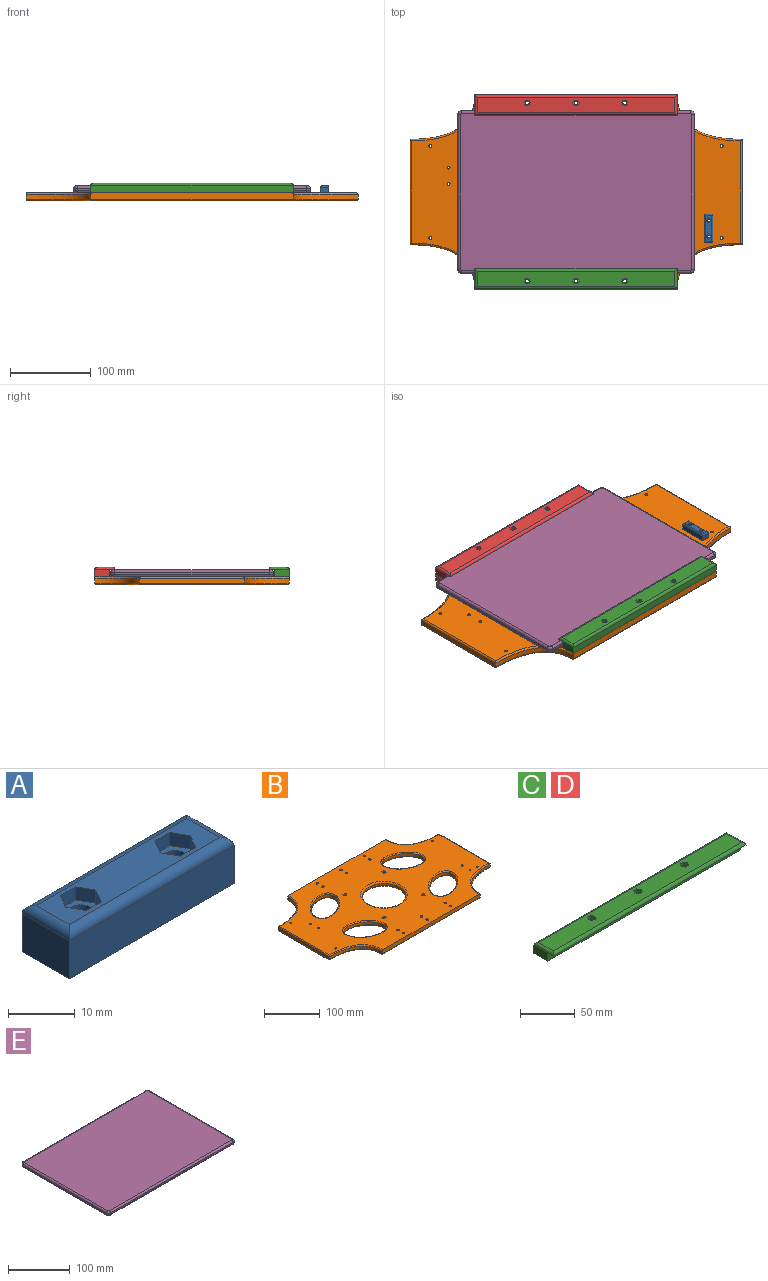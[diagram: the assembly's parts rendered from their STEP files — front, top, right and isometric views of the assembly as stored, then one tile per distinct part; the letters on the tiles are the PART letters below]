
ASSEMBLY  parts=5 mates=4
PART A: 26 faces, bbox 35x10x8.5 mm
  f0: cylinder r=1.8mm len=6.1mm, axis (0,0,1), area 69mm2, adj f6,f25
  f1: cylinder r=1.8mm len=6.1mm, axis (0,0,1), area 69mm2, adj f6,f18
  f2: plane 35x7mm, normal (0,-1,0), area 245mm2, adj f3,f5,f6,f8
  f3: plane 10x7mm, normal (1,0,0), area 70mm2, adj f2,f4,f6,f9
  f4: plane 35x7mm, normal (0,1,0), area 245mm2, adj f3,f5,f6,f11
  f5: plane 10x7mm, normal (-1,0,0), area 70mm2, adj f2,f4,f6,f10
  f6: plane 35x10mm, normal (0,0,-1), area 329.6mm2, adj f0,f1,f2,f3,f4,f5
  f7: plane 32x7mm, normal (0,0,1), area 171.6mm2, adj f8,f9,f10,f11,f12,f13,f14,f15
  f8: cylinder r=1.5mm len=35mm, axis (1,0,0), area 79.9mm2, adj f2,f7,f9,f10
  f9: cylinder r=1.5mm len=10mm, axis (0,1,0), area 21mm2, adj f3,f7,f8,f11
  f10: cylinder r=1.5mm len=10mm, axis (0,-1,0), area 21mm2, adj f5,f7,f8,f11
  f11: cylinder r=1.5mm len=35mm, axis (-1,0,0), area 79.9mm2, adj f4,f7,f9,f10
  f12: plane 2.75x2.4mm, normal (-0.87,0.5,0), area 7.6mm2, adj f7,f13,f17,f18
  f13: plane 2.75x2.4mm, normal (-0.87,-0.5,0), area 7.6mm2, adj f7,f12,f14,f18
  f14: plane 3.18x2.4mm, normal (0,-1,0), area 7.6mm2, adj f7,f13,f15,f18
  f15: plane 2.75x2.4mm, normal (0.87,-0.5,0), area 7.6mm2, adj f7,f14,f16,f18
  f16: plane 2.75x2.4mm, normal (0.87,0.5,0), area 7.6mm2, adj f7,f15,f17,f18
  f17: plane 3.18x2.4mm, normal (0,1,0), area 7.6mm2, adj f7,f12,f16,f18
  f18: plane 6.35x5.5mm, normal (0,0,1), area 16mm2, adj f1,f12,f13,f14,f15,f16,f17
  f19: plane 2.75x2.4mm, normal (0.87,-0.5,0), area 7.6mm2, adj f7,f20,f24,f25
  f20: plane 2.75x2.4mm, normal (0.87,0.5,0), area 7.6mm2, adj f7,f19,f21,f25
  f21: plane 3.18x2.4mm, normal (0,1,0), area 7.6mm2, adj f7,f20,f22,f25
  f22: plane 2.75x2.4mm, normal (-0.87,0.5,0), area 7.6mm2, adj f7,f21,f23,f25
  f23: plane 2.75x2.4mm, normal (-0.87,-0.5,0), area 7.6mm2, adj f7,f22,f24,f25
  f24: plane 3.18x2.4mm, normal (0,-1,0), area 7.6mm2, adj f7,f19,f23,f25
  f25: plane 6.35x5.5mm, normal (0,0,1), area 16mm2, adj f0,f19,f20,f21,f22,f23,f24
PART B: 123 faces, bbox 413.3x241.5x10.1 mm
  f0: plane 406.06x240.06mm, normal (0,0,1), area 63187.4mm2, adj f8,f15,f18,f29,f30,f31,f32,f33
  f1: cylinder r=2.4mm len=6mm, axis (0,0,1), area 90.5mm2, adj f9,f86
  f2: cylinder r=2.4mm len=6mm, axis (0,0,1), area 90.5mm2, adj f9,f79
  f3: cylinder r=2.4mm len=6mm, axis (0,0,1), area 90.5mm2, adj f9,f72
  f4: cylinder r=2.4mm len=6mm, axis (0,0,1), area 90.5mm2, adj f9,f65
  f5: extruded ~80x55mm, area 661.9mm2, adj f6,f8,f20,f29
  f6: plane 130x6mm, normal (-1,0,0), area 780mm2, adj f5,f13,f22,f30
  f7: extruded ~70.11x57.36mm, area 1193.2mm2, adj f38,f39
  f8: plane 250.06x8.06mm, normal (0,1,0), area 1998.3mm2, adj f0,f5,f10,f21,f29,f33
  f9: plane 406.06x236.06mm, normal (0,0,-1), area 61751.9mm2, adj f1,f2,f3,f4,f19,f20,f21,f22
  f10: extruded ~80x55mm, area 661.9mm2, adj f8,f11,f23,f33
  f11: plane 130x6mm, normal (1,0,0), area 780mm2, adj f10,f16,f25,f34
  f12: extruded ~70.3x57.3mm, area 1193.2mm2, adj f36,f37
  f13: extruded ~80x55mm, area 661.9mm2, adj f6,f15,f24,f31
  f14: extruded ~70.3x57.3mm, area 1193.2mm2, adj f18,f28
  f15: plane 250.06x8.06mm, normal (0,-1,0), area 1998.3mm2, adj f0,f13,f16,f26,f31,f35
  f16: extruded ~80x55mm, area 661.9mm2, adj f11,f15,f27,f35
  f17: extruded ~70.11x57.36mm, area 1193.2mm2, adj f19,f32
  f18: bspline ~74.32x61.43mm, area 639.2mm2, adj f0,f14
  f19: bspline ~74.35x61.42mm, area 639.2mm2, adj f9,f17
  f20: bspline ~83.64x57.72mm, area 343.9mm2, adj f5,f9,f21,f22
  f21: cylinder r=2mm len=250mm, axis (-1,0,0), area 779.2mm2, adj f8,f9,f20,f23
  f22: cylinder r=2mm len=130mm, axis (0,-1,0), area 402.2mm2, adj f6,f9,f20,f24
  f23: bspline ~83.64x57.72mm, area 343.9mm2, adj f9,f10,f21,f25
  f24: bspline ~83.64x57.72mm, area 343.9mm2, adj f9,f13,f22,f26
  f25: cylinder r=2mm len=130mm, axis (0,-1,0), area 402.2mm2, adj f9,f11,f23,f27
  f26: cylinder r=2mm len=250mm, axis (-1,0,0), area 779.2mm2, adj f9,f15,f24,f27
  f27: bspline ~83.64x57.72mm, area 343.9mm2, adj f9,f16,f25,f26
  f28: bspline ~74.35x61.42mm, area 639.2mm2, adj f9,f14
  f29: bspline ~83.64x57.72mm, area 347mm2, adj f0,f5,f8,f30
  f30: cylinder r=2mm len=130mm, axis (0,1,0), area 402.2mm2, adj f0,f6,f29,f31
  f31: bspline ~83.64x57.72mm, area 347mm2, adj f0,f13,f15,f30
  f32: bspline ~74.32x61.43mm, area 639.2mm2, adj f0,f17
  f33: bspline ~83.64x57.72mm, area 347mm2, adj f0,f8,f10,f34
  f34: cylinder r=2mm len=130mm, axis (0,1,0), area 402.2mm2, adj f0,f11,f33,f35
  f35: bspline ~83.64x57.72mm, area 347mm2, adj f0,f15,f16,f34
  f36: bspline ~74.32x61.43mm, area 639.2mm2, adj f0,f12
  f37: bspline ~74.35x61.42mm, area 639.2mm2, adj f9,f12
  f38: bspline ~74.35x61.42mm, area 639.2mm2, adj f7,f9
  f39: bspline ~74.32x61.43mm, area 639.2mm2, adj f0,f7
  f40: cylinder r=1.8mm len=10mm, axis (0,0,1), area 113.1mm2, adj f0,f9
  f41: cylinder r=1.8mm len=10mm, axis (0,0,1), area 113.1mm2, adj f0,f9
  f42: cylinder r=1.8mm len=10mm, axis (0,0,1), area 113.1mm2, adj f0,f9
  f43: cylinder r=1.8mm len=10mm, axis (0,0,1), area 113.1mm2, adj f0,f9
  f44: cylinder r=39.02mm len=78.04mm, axis (0,0,1), area 980.6mm2, adj f45,f46
  f45: torus R=42.02mm, axis (0,0,1), area 1187.5mm2, adj f9,f44
  f46: torus R=42.02mm, axis (0,0,1), area 1187.5mm2, adj f0,f44
  f47: cylinder r=1.7mm len=7mm, axis (0,0,-1), area 74.8mm2, adj f0,f48
  f48: plane 6.5x6.5mm, normal (0,0,-1), area 24.1mm2, adj f47,f49
  f49: cylinder r=3.25mm len=6.5mm, axis (0,0,-1), area 61.3mm2, adj f9,f48
  f50: cylinder r=1.7mm len=7mm, axis (0,0,-1), area 74.8mm2, adj f0,f51
  f51: plane 6.5x6.5mm, normal (0,0,-1), area 24.1mm2, adj f50,f52
  f52: cylinder r=3.25mm len=6.5mm, axis (0,0,-1), area 61.3mm2, adj f9,f51
  f53: cylinder r=1.7mm len=7mm, axis (0,0,-1), area 74.8mm2, adj f0,f54
  f54: plane 6.5x6.5mm, normal (0,0,-1), area 24.1mm2, adj f53,f55
  f55: cylinder r=3.25mm len=6.5mm, axis (0,0,-1), area 61.3mm2, adj f9,f54
  f56: cylinder r=1.7mm len=7mm, axis (0,0,-1), area 74.8mm2, adj f0,f57
  f57: plane 6.5x6.5mm, normal (0,0,-1), area 24.1mm2, adj f56,f58
  f58: cylinder r=3.25mm len=6.5mm, axis (0,0,-1), area 61.3mm2, adj f9,f57
  f59: plane 4x3.5mm, normal (-0.87,0.5,0), area 16.2mm2, adj f0,f60,f64,f65
  f60: plane 4x3.5mm, normal (-0.87,-0.5,0), area 16.2mm2, adj f0,f59,f61,f65
  f61: plane 4.04x4mm, normal (0,-1,0), area 16.2mm2, adj f0,f60,f62,f65
  f62: plane 4x3.5mm, normal (0.87,-0.5,0), area 16.2mm2, adj f0,f61,f63,f65
  f63: plane 4x3.5mm, normal (0.87,0.5,0), area 16.2mm2, adj f0,f62,f64,f65
  f64: plane 4.04x4mm, normal (0,1,0), area 16.2mm2, adj f0,f59,f63,f65
  f65: plane 8.08x7mm, normal (0,0,1), area 24.3mm2, adj f4,f59,f60,f61,f62,f63,f64
  f66: plane 4x3.5mm, normal (-0.87,-0.5,0), area 16.2mm2, adj f0,f67,f71,f72
  f67: plane 4.04x4mm, normal (0,-1,0), area 16.2mm2, adj f0,f66,f68,f72
  f68: plane 4x3.5mm, normal (0.87,-0.5,0), area 16.2mm2, adj f0,f67,f69,f72
  f69: plane 4x3.5mm, normal (0.87,0.5,0), area 16.2mm2, adj f0,f68,f70,f72
  f70: plane 4.04x4mm, normal (0,1,0), area 16.2mm2, adj f0,f69,f71,f72
  f71: plane 4x3.5mm, normal (-0.87,0.5,0), area 16.2mm2, adj f0,f66,f70,f72
  f72: plane 8.08x7mm, normal (0,0,1), area 24.3mm2, adj f3,f66,f67,f68,f69,f70,f71
  f73: plane 4x3.5mm, normal (0.87,-0.5,0), area 16.2mm2, adj f0,f74,f78,f79
  f74: plane 4x3.5mm, normal (0.87,0.5,0), area 16.2mm2, adj f0,f73,f75,f79
  f75: plane 4.04x4mm, normal (0,1,0), area 16.2mm2, adj f0,f74,f76,f79
  f76: plane 4x3.5mm, normal (-0.87,0.5,0), area 16.2mm2, adj f0,f75,f77,f79
  f77: plane 4x3.5mm, normal (-0.87,-0.5,0), area 16.2mm2, adj f0,f76,f78,f79
  f78: plane 4.04x4mm, normal (0,-1,0), area 16.2mm2, adj f0,f73,f77,f79
  f79: plane 8.08x7mm, normal (0,0,1), area 24.3mm2, adj f2,f73,f74,f75,f76,f77,f78
  f80: plane 4.04x4mm, normal (0,1,0), area 16.2mm2, adj f0,f81,f85,f86
  f81: plane 4x3.5mm, normal (-0.87,0.5,0), area 16.2mm2, adj f0,f80,f82,f86
  f82: plane 4x3.5mm, normal (-0.87,-0.5,0), area 16.2mm2, adj f0,f81,f83,f86
  f83: plane 4.04x4mm, normal (0,-1,0), area 16.2mm2, adj f0,f82,f84,f86
  f84: plane 4x3.5mm, normal (0.87,-0.5,0), area 16.2mm2, adj f0,f83,f85,f86
  f85: plane 4x3.5mm, normal (0.87,0.5,0), area 16.2mm2, adj f0,f80,f84,f86
  f86: plane 8.08x7mm, normal (0,0,1), area 24.3mm2, adj f1,f80,f81,f82,f83,f84,f85
  f87: cylinder r=2.25mm len=6mm, axis (0,0,-1), area 84.8mm2, adj f0,f88
  f88: plane 8.25x8.25mm, normal (0,0,-1), area 37.6mm2, adj f87,f89
  f89: cylinder r=4.12mm len=8.25mm, axis (0,0,-1), area 103.7mm2, adj f9,f88
  f90: cylinder r=2.25mm len=6mm, axis (0,0,-1), area 84.8mm2, adj f0,f91
  f91: plane 8.25x8.25mm, normal (0,0,-1), area 37.6mm2, adj f90,f92
  f92: cylinder r=4.12mm len=8.25mm, axis (0,0,-1), area 103.7mm2, adj f9,f91
  f93: cylinder r=2.25mm len=6mm, axis (0,0,-1), area 84.8mm2, adj f0,f94
  f94: plane 8.25x8.25mm, normal (0,0,-1), area 37.6mm2, adj f93,f95
  f95: cylinder r=4.12mm len=8.25mm, axis (0,0,-1), area 103.7mm2, adj f9,f94
  f96: cylinder r=2.25mm len=6mm, axis (0,0,-1), area 84.8mm2, adj f0,f97
  f97: plane 8.25x8.25mm, normal (0,0,-1), area 37.6mm2, adj f96,f98
  f98: cylinder r=4.12mm len=8.25mm, axis (0,0,-1), area 103.7mm2, adj f9,f97
  f99: cylinder r=2.25mm len=6mm, axis (0,0,-1), area 84.8mm2, adj f0,f100
  f100: plane 8.25x8.25mm, normal (0,0,-1), area 37.6mm2, adj f99,f101
  f101: cylinder r=4.12mm len=8.25mm, axis (0,0,-1), area 103.7mm2, adj f9,f100
  f102: cylinder r=2.25mm len=6mm, axis (0,0,-1), area 84.8mm2, adj f0,f103
  f103: plane 8.25x8.25mm, normal (0,0,-1), area 37.6mm2, adj f102,f104
  f104: cylinder r=4.12mm len=8.25mm, axis (0,0,-1), area 103.7mm2, adj f9,f103
  f105: cylinder r=2.25mm len=6mm, axis (0,0,-1), area 84.8mm2, adj f0,f106
  f106: plane 8.25x8.25mm, normal (0,0,-1), area 37.6mm2, adj f105,f107
  f107: cylinder r=4.12mm len=8.25mm, axis (0,0,-1), area 103.7mm2, adj f9,f106
  f108: cylinder r=2.25mm len=6mm, axis (0,0,-1), area 84.8mm2, adj f0,f109
  f109: plane 8.25x8.25mm, normal (0,0,-1), area 37.6mm2, adj f108,f110
  f110: cylinder r=4.12mm len=8.25mm, axis (0,0,-1), area 103.7mm2, adj f9,f109
  f111: cylinder r=2.25mm len=6mm, axis (0,0,-1), area 84.8mm2, adj f0,f112
  f112: plane 8.25x8.25mm, normal (0,0,-1), area 37.6mm2, adj f111,f113
  f113: cylinder r=4.12mm len=8.25mm, axis (0,0,-1), area 103.7mm2, adj f9,f112
  f114: cylinder r=2.25mm len=6mm, axis (0,0,-1), area 84.8mm2, adj f0,f115
  f115: plane 8.25x8.25mm, normal (0,0,-1), area 37.6mm2, adj f114,f116
  f116: cylinder r=4.12mm len=8.25mm, axis (0,0,-1), area 103.7mm2, adj f9,f115
  f117: cylinder r=2.25mm len=6mm, axis (0,0,-1), area 84.8mm2, adj f0,f118
  f118: plane 8.25x8.25mm, normal (0,0,-1), area 37.6mm2, adj f117,f119
  f119: cylinder r=4.12mm len=8.25mm, axis (0,0,-1), area 103.7mm2, adj f9,f118
  f120: cylinder r=2.25mm len=6mm, axis (0,0,-1), area 84.8mm2, adj f0,f121
  f121: plane 8.25x8.25mm, normal (0,0,-1), area 37.6mm2, adj f120,f122
  f122: cylinder r=4.12mm len=8.25mm, axis (0,0,-1), area 103.7mm2, adj f9,f121
PART C: 35 faces, bbox 250x25x12 mm
  f0: plane 244x19mm, normal (0,0,1), area 4508.7mm2, adj f10,f11,f12,f13,f14,f15,f16,f17
  f1: cylinder r=2.4mm len=8.8mm, axis (0,0,1), area 132.7mm2, adj f6,f34
  f2: cylinder r=2.4mm len=8.8mm, axis (0,0,1), area 132.7mm2, adj f6,f27
  f3: cylinder r=2.4mm len=8.8mm, axis (0,0,1), area 132.7mm2, adj f6,f20
  f4: plane 18x9mm, normal (-1,0,0), area 162mm2, adj f5,f6,f9,f10
  f5: plane 250x9mm, normal (0,1,0), area 2250mm2, adj f4,f6,f7,f11
  f6: plane 250x18mm, normal (0,0,-1), area 4445.7mm2, adj f1,f2,f3,f4,f5,f7,f9
  f7: plane 18x9mm, normal (1,0,0), area 162mm2, adj f5,f6,f9,f13
  f8: plane 250x7mm, normal (0,0,-1), area 1750mm2, adj f9,f10,f12,f13
  f9: plane 250x9mm, normal (0,-1,0), area 2250mm2, adj f4,f6,f7,f8
  f10: cylinder r=3mm len=25mm, axis (0,1,0), area 107.5mm2, adj f0,f4,f8,f11,f12
  f11: cylinder r=3mm len=250mm, axis (1,0,0), area 1167.8mm2, adj f0,f5,f10,f13
  f12: cylinder r=3mm len=250mm, axis (-1,0,0), area 1167.8mm2, adj f0,f8,f10,f13
  f13: cylinder r=3mm len=25mm, axis (0,1,0), area 107.5mm2, adj f0,f7,f8,f11,f12
  f14: plane 4.04x3.2mm, normal (0,1,0), area 12.9mm2, adj f0,f15,f19,f20
  f15: plane 3.5x3.2mm, normal (-0.87,0.5,0), area 12.9mm2, adj f0,f14,f16,f20
  f16: plane 3.5x3.2mm, normal (-0.87,-0.5,0), area 12.9mm2, adj f0,f15,f17,f20
  f17: plane 4.04x3.2mm, normal (0,-1,0), area 12.9mm2, adj f0,f16,f18,f20
  f18: plane 3.5x3.2mm, normal (0.87,-0.5,0), area 12.9mm2, adj f0,f17,f19,f20
  f19: plane 3.5x3.2mm, normal (0.87,0.5,0), area 12.9mm2, adj f0,f14,f18,f20
  f20: plane 8.08x7mm, normal (0,0,1), area 24.3mm2, adj f3,f14,f15,f16,f17,f18,f19
  f21: plane 4.04x3.2mm, normal (0,1,0), area 12.9mm2, adj f0,f22,f26,f27
  f22: plane 3.5x3.2mm, normal (-0.87,0.5,0), area 12.9mm2, adj f0,f21,f23,f27
  f23: plane 3.5x3.2mm, normal (-0.87,-0.5,0), area 12.9mm2, adj f0,f22,f24,f27
  f24: plane 4.04x3.2mm, normal (0,-1,0), area 12.9mm2, adj f0,f23,f25,f27
  f25: plane 3.5x3.2mm, normal (0.87,-0.5,0), area 12.9mm2, adj f0,f24,f26,f27
  f26: plane 3.5x3.2mm, normal (0.87,0.5,0), area 12.9mm2, adj f0,f21,f25,f27
  f27: plane 8.08x7mm, normal (0,0,1), area 24.3mm2, adj f2,f21,f22,f23,f24,f25,f26
  f28: plane 3.5x3.2mm, normal (-0.87,0.5,0), area 12.9mm2, adj f0,f29,f33,f34
  f29: plane 3.5x3.2mm, normal (-0.87,-0.5,0), area 12.9mm2, adj f0,f28,f30,f34
  f30: plane 4.04x3.2mm, normal (0,-1,0), area 12.9mm2, adj f0,f29,f31,f34
  f31: plane 3.5x3.2mm, normal (0.87,-0.5,0), area 12.9mm2, adj f0,f30,f32,f34
  f32: plane 3.5x3.2mm, normal (0.87,0.5,0), area 12.9mm2, adj f0,f31,f33,f34
  f33: plane 4.04x3.2mm, normal (0,1,0), area 12.9mm2, adj f0,f28,f32,f34
  f34: plane 8.08x7mm, normal (0,0,1), area 24.3mm2, adj f1,f28,f29,f30,f31,f32,f33
PART D: same geometry as C
PART E: 26 faces, bbox 292x201x8.5 mm
  f0: plane 282x2.5mm, normal (0,1,0), area 705mm2, adj f1,f5,f10,f20
  f1: cylinder r=5mm len=5mm, axis (0,0,-1), area 19.6mm2, adj f0,f2,f11,f18
  f2: plane 191x2.5mm, normal (-1,0,0), area 477.5mm2, adj f1,f8,f13,f19
  f3: plane 286x195mm, normal (0,0,1), area 55766.6mm2, adj f10,f11,f12,f13,f14,f15,f16,f17
  f4: plane 286x195mm, normal (0,0,-1), area 55766.6mm2, adj f18,f19,f20,f21,f22,f23,f24,f25
  f5: cylinder r=5mm len=5mm, axis (0,0,-1), area 19.6mm2, adj f0,f6,f12,f22
  f6: plane 191x2.5mm, normal (1,0,0), area 477.5mm2, adj f5,f9,f14,f24
  f7: plane 282x2.5mm, normal (0,-1,0), area 705mm2, adj f8,f9,f17,f23
  f8: cylinder r=5mm len=5mm, axis (0,0,-1), area 19.6mm2, adj f2,f7,f15,f21
  f9: cylinder r=5mm len=5mm, axis (0,0,-1), area 19.6mm2, adj f6,f7,f16,f25
  f10: cylinder r=3mm len=282mm, axis (1,0,0), area 1328.9mm2, adj f0,f3,f11,f12
  f11: torus R=2mm, axis (0,0,1), area 28.9mm2, adj f1,f3,f10,f13
  f12: torus R=2mm, axis (0,0,1), area 28.9mm2, adj f3,f5,f10,f14
  f13: cylinder r=3mm len=191mm, axis (0,1,0), area 900.1mm2, adj f2,f3,f11,f15
  f14: cylinder r=3mm len=191mm, axis (0,1,0), area 900.1mm2, adj f3,f6,f12,f16
  f15: torus R=2mm, axis (0,0,1), area 28.9mm2, adj f3,f8,f13,f17
  f16: torus R=2mm, axis (0,0,1), area 28.9mm2, adj f3,f9,f14,f17
  f17: cylinder r=3mm len=282mm, axis (1,0,0), area 1328.9mm2, adj f3,f7,f15,f16
  f18: torus R=2mm, axis (0,0,1), area 28.9mm2, adj f1,f4,f19,f20
  f19: cylinder r=3mm len=191mm, axis (0,-1,0), area 900.1mm2, adj f2,f4,f18,f21
  f20: cylinder r=3mm len=282mm, axis (-1,0,0), area 1328.9mm2, adj f0,f4,f18,f22
  f21: torus R=2mm, axis (0,0,1), area 28.9mm2, adj f4,f8,f19,f23
  f22: torus R=2mm, axis (0,0,1), area 28.9mm2, adj f4,f5,f20,f24
  f23: cylinder r=3mm len=282mm, axis (-1,0,0), area 1328.9mm2, adj f4,f7,f21,f25
  f24: cylinder r=3mm len=191mm, axis (0,-1,0), area 900.1mm2, adj f4,f6,f22,f25
  f25: torus R=2mm, axis (0,0,1), area 28.9mm2, adj f4,f9,f23,f24
PLACE A rot(axis=(0,0,1),90deg) t=(169,-27.5,18.5)mm
PLACE B at identity
PLACE C rot(axis=(0,0,1),180deg) t=(0,-95,10)mm
PLACE D t=(0,95,10)mm
PLACE E rot(axis=(0,1,0),180deg) t=(0,0,18.5)mm
MATE fastened B.f47 <-> A.f0  axis (0,0,1) through (164,-35,10)mm
MATE fastened B.f93 <-> D.f2  axis (0,0,1) through (0,110,10)mm
MATE planar B.f0 <-> E.f3  axis (0,0,1) through (-0.01,0.01,10)mm
MATE fastened C.f2 <-> B.f102  axis (0,0,-1) through (0,-110,10)mm
